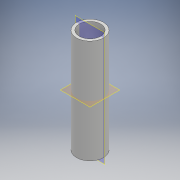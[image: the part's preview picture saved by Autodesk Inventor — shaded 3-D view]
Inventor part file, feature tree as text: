
AUTODESK INVENTOR PART (.ipt)
format: ipt  version: 2017 (Build 210142000, 142)  size: 96,256 bytes
history: native  units: mm
features: extrude x1, sketch x1
ambient origin geometry x8: Origin, YZ Plane, XZ Plane, XY Plane, X Axis, Y Axis, Z Axis, Center Point
bodies: Solid1 (feature_tree)
feature tree (2):
  extrude  "Extrusion1"  Depth=100.0mm
  sketch  "Sketch1"  dims[d0=26.0mm d1=2.7mm d2=100.0mm d3=0.0mm]
